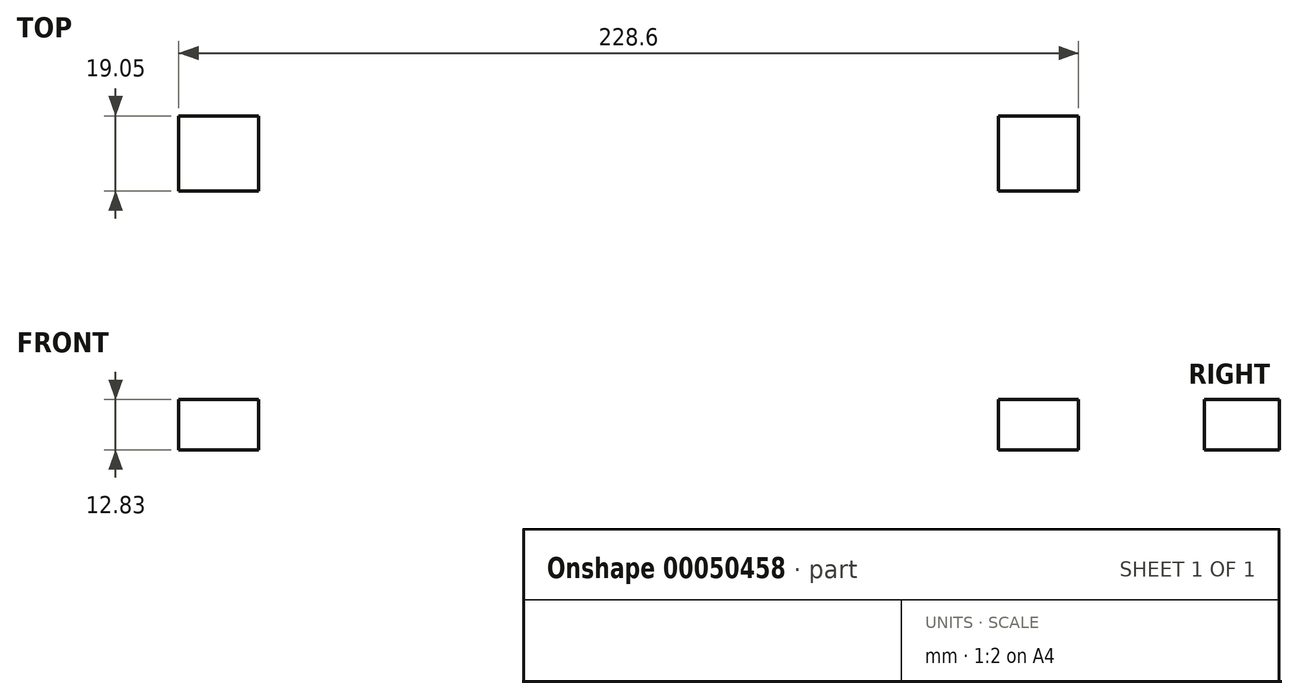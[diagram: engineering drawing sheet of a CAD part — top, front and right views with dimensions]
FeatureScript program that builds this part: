
annotation { "Feature Type Name" : "Feature", "Feature Type Description" : "" }
export const myFeature = defineFeature(function(context is Context, id is Id, definition is map)
    precondition{}
    {
        {
            var Q0;
            Q0=qCreatedBy(makeId("Front.planeOp"),FACE);
            var sketch = newSketch(context, id + "F0", { "sketchPlane" : qUnion([Q0])});
            skLineSegment(sketch, "E0.rect.bottom", {"start": v(114.3, 19.05) * mm, "end": v(-114.3, 19.05) * mm});
            skLineSegment(sketch, "E0.rect.top", {"start": v(114.3, -19.05) * mm, "end": v(-114.3, -19.05) * mm});
            skLineSegment(sketch, "E0.rect.left", {"start": v(114.3, 19.05) * mm, "end": v(114.3, -19.05) * mm});
            skLineSegment(sketch, "E0.rect.right", {"start": v(-114.3, 19.05) * mm, "end": v(-114.3, -19.05) * mm});
            skPoint(sketch, "E0.rect.middle", {"position": v(0, 0) * mm});
            skLineSegment(sketch, "E1.bottom", {"start": v(-114.3, 19.05) * mm, "end": v(-93.98, 19.05) * mm});
            skLineSegment(sketch, "E1.top", {"start": v(-114.3, 6.22) * mm, "end": v(-93.98, 6.22) * mm});
            skLineSegment(sketch, "E1.left", {"start": v(-114.3, 19.05) * mm, "end": v(-114.3, 6.22) * mm});
            skLineSegment(sketch, "E1.right", {"start": v(-93.98, 19.05) * mm, "end": v(-93.98, 6.22) * mm});
            skLineSegment(sketch, "E2.bottom", {"start": v(-114.3, -19.05) * mm, "end": v(-93.98, -19.05) * mm});
            skLineSegment(sketch, "E2.top", {"start": v(-114.3, -6.22) * mm, "end": v(-93.98, -6.22) * mm});
            skLineSegment(sketch, "E2.left", {"start": v(-114.3, -19.05) * mm, "end": v(-114.3, -6.22) * mm});
            skLineSegment(sketch, "E2.right", {"start": v(-93.98, -19.05) * mm, "end": v(-93.98, -6.22) * mm});
            skLineSegment(sketch, "E3.MirrorCS", {"start": v(93.98, 19.05) * mm, "end": v(93.98, 6.22) * mm});
            skLineSegment(sketch, "E4.MirrorCS", {"start": v(114.3, 6.22) * mm, "end": v(93.98, 6.22) * mm});
            skLineSegment(sketch, "E5.MirrorCS", {"start": v(114.3, 19.05) * mm, "end": v(114.3, 6.22) * mm});
            skLineSegment(sketch, "E6.MirrorCS", {"start": v(114.3, 19.05) * mm, "end": v(93.98, 19.05) * mm});
            skLineSegment(sketch, "E7.MirrorCS", {"start": v(114.3, -6.22) * mm, "end": v(93.98, -6.22) * mm});
            skLineSegment(sketch, "E8.MirrorCS", {"start": v(114.3, -19.05) * mm, "end": v(114.3, -6.22) * mm});
            skLineSegment(sketch, "E9.MirrorCS", {"start": v(114.3, -19.05) * mm, "end": v(93.98, -19.05) * mm});
            skLineSegment(sketch, "E10.MirrorCS", {"start": v(93.98, -19.05) * mm, "end": v(93.98, -6.22) * mm});
            skSolve(sketch);
        }
        {
            var Q0;
            Q0=makeQuery(id+"F0.imprint","IMPRINT",FACE,{"disambiguationData":[TD([[makeQuery(id+"F0.imprint","IMPRINT",EDGE,{"derivedFrom":sQuery(id+"F0.wireOp",EDGE,"E0.rect.bottom")}),1.0]])]});
            extrude(context, id + "F1", {"entities" : qUnion([Q0]), "depth" : 19.05 * mm});
        }
        {
            var Q0;
            Q0=makeQuery(id+"F1.opExtrude","SWEPT_FACE",FACE,{"disambiguationData":[OSD([sQuery(id+"F0.wireOp",EDGE,"E1.top")])]});
            var sketch = newSketch(context, id + "F2", { "sketchPlane" : qUnion([Q0])});
            skPoint(sketch, "E11", {"position": v(-106.68, -9.53) * mm});
            skPoint(sketch, "E11.positionSnap0", {"position": v(-114.3, -9.53) * mm});
            skPoint(sketch, "E12.MirrorP", {"position": v(106.68, -9.53) * mm});
            skSolve(sketch);
        }
        {
            var Q0;
            Q0=sQuery(id+"F2.wireOp",VERTEX,"E11");
            var Q1;
            Q1=sQuery(id+"F2.wireOp",VERTEX,"E12.MirrorP");
            var Q2;
            Q2=makeQuery(id+"F1.opExtrude","SWEPT_BODY",BODY,{"disambiguationData":[OSD([sQuery(id+"F0.wireOp",EDGE,"E0.rect.bottom"),sQuery(id+"F0.wireOp",EDGE,"E0.rect.top"),sQuery(id+"F0.wireOp",EDGE,"E0.rect.left"),sQuery(id+"F0.wireOp",EDGE,"E0.rect.right"),sQuery(id+"F0.wireOp",EDGE,"E1.top"),sQuery(id+"F0.wireOp",EDGE,"E1.right"),sQuery(id+"F0.wireOp",EDGE,"E2.top"),sQuery(id+"F0.wireOp",EDGE,"E2.right"),sQuery(id+"F0.wireOp",EDGE,"E3.MirrorCS"),sQuery(id+"F0.wireOp",EDGE,"E4.MirrorCS"),sQuery(id+"F0.wireOp",EDGE,"E7.MirrorCS"),sQuery(id+"F0.wireOp",EDGE,"E10.MirrorCS")])]});
            hole(context, id + "F3", {"style" : HoleStyle.SIMPLE, "holeDiameter" : 6.35 * mm, "endStyle" : HoleEndStyle.THROUGH, "locations" : qUnion([Q0, Q1]), "scope" : qUnion([Q2])});
        }
        {
            var Q0;
            Q0=makeQuery(id+"F1.opExtrude","CAP_FACE",FACE,{"disambiguationData":[OSD([sQuery(id+"F0.wireOp",EDGE,"E0.rect.bottom"),sQuery(id+"F0.wireOp",EDGE,"E0.rect.top"),sQuery(id+"F0.wireOp",EDGE,"E0.rect.left"),sQuery(id+"F0.wireOp",EDGE,"E0.rect.right"),sQuery(id+"F0.wireOp",EDGE,"E1.top"),sQuery(id+"F0.wireOp",EDGE,"E1.right"),sQuery(id+"F0.wireOp",EDGE,"E2.top"),sQuery(id+"F0.wireOp",EDGE,"E2.right"),sQuery(id+"F0.wireOp",EDGE,"E3.MirrorCS"),sQuery(id+"F0.wireOp",EDGE,"E4.MirrorCS"),sQuery(id+"F0.wireOp",EDGE,"E7.MirrorCS"),sQuery(id+"F0.wireOp",EDGE,"E10.MirrorCS")])],"isStart":false});
            var sketch = newSketch(context, id + "F4", { "sketchPlane" : qUnion([Q0])});
            skFitSpline(sketch, "E13", {"points": [v(-81.28, 19.05) * mm, v(-55.88, 6.35) * mm, v(0, 19.05) * mm, v(55.88, 6.35) * mm, v(81.28, 19.05) * mm], "startDerivative": vector(178.42, -101.86) * mm, "endDerivative": vector(132.57, 105.85) * mm});
            skLineSegment(sketch, "E14", {"start": v(-81.28, 19.05) * mm, "end": v(81.28, 19.05) * mm});
            skFitSpline(sketch, "E15.MirrorCS", {"points": [v(-81.28, -19.05) * mm, v(-55.88, -6.35) * mm, v(0, -19.05) * mm, v(55.88, -6.35) * mm, v(81.28, -19.05) * mm], "startDerivative": vector(178.42, 101.86) * mm, "endDerivative": vector(132.57, -105.85) * mm});
            skLineSegment(sketch, "E16.MirrorCS", {"start": v(-81.28, -19.05) * mm, "end": v(81.28, -19.05) * mm});
            skSolve(sketch);
        }
        {
            var Q0;
            Q0 = qSketchRegion(id + "F4", true);
            extrude(context, id + "F5", {"entities" : qUnion([Q0]), "operationType" : NewBodyOperationType.REMOVE, "oppositeDirection" : true, "depth" : 25.4 * mm});
        }
    });
